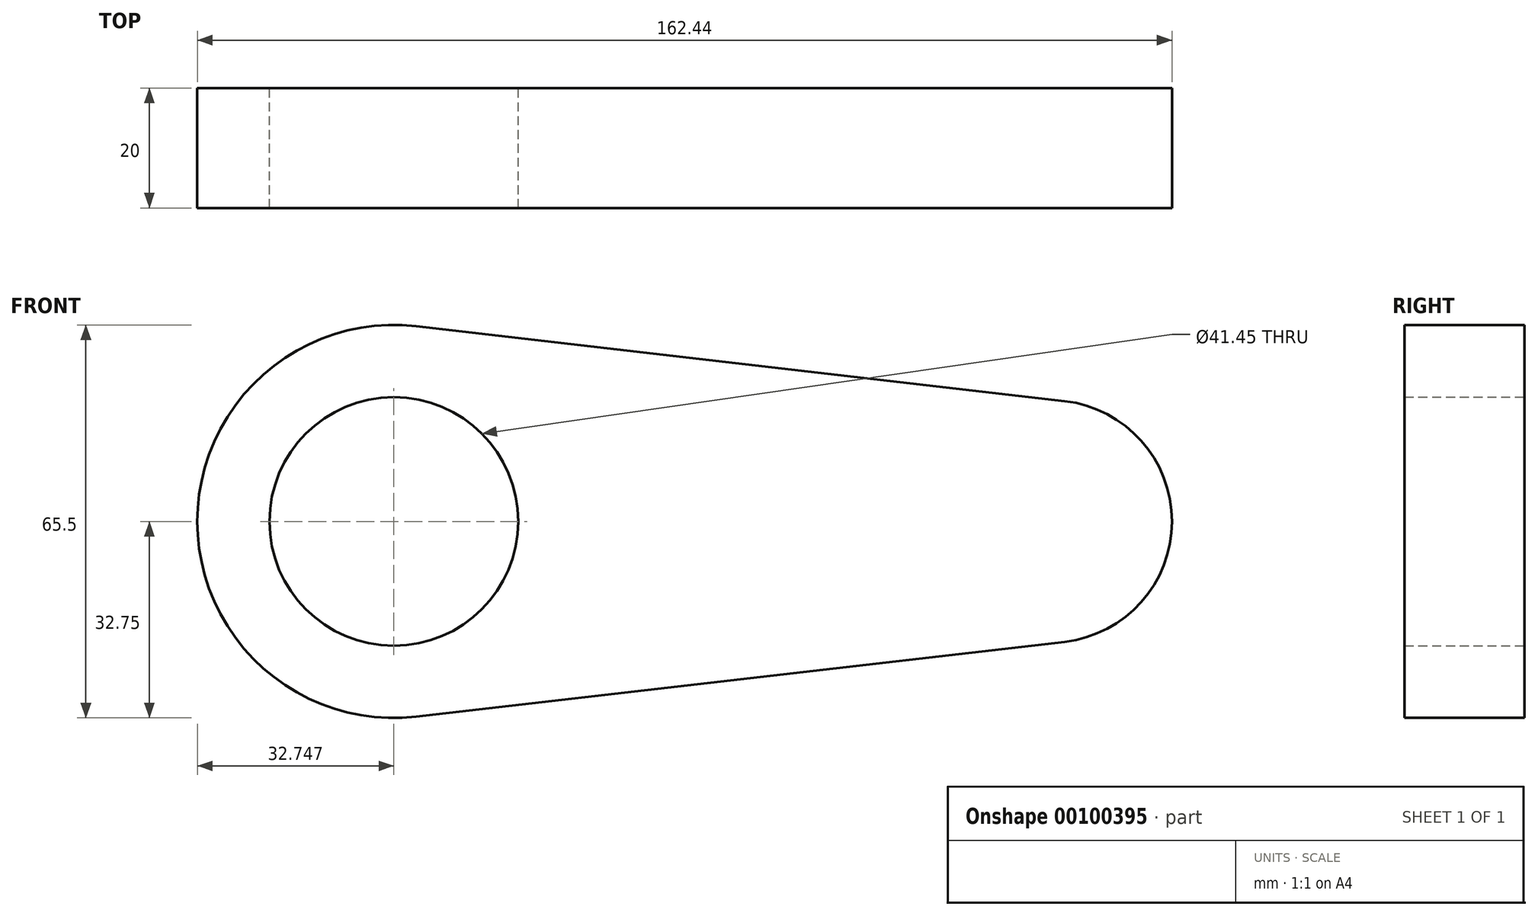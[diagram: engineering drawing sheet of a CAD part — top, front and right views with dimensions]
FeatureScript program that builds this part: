
annotation { "Feature Type Name" : "Feature", "Feature Type Description" : "" }
export const myFeature = defineFeature(function(context is Context, id is Id, definition is map)
    precondition{}
    {
        {
            var Q0;
            Q0=qCreatedBy(makeId("Front.planeOp"),FACE);
            var sketch = newSketch(context, id + "F0", { "sketchPlane" : qUnion([Q0])});
            skCircle(sketch, "E0", {"center": v(-65.7, 0) * mm, "radius": 20.72 * mm});
            skCircle(sketch, "E1", {"center": v(-65.7, 0) * mm, "radius": 32.75 * mm});
            skCircle(sketch, "E2", {"center": v(43.8, 0) * mm, "radius": 20.2 * mm});
            skLineSegment(sketch, "E3", {"start": v(-61.94, 32.53) * mm, "end": v(46.11, 20.07) * mm});
            skLineSegment(sketch, "E4", {"start": v(-61.94, -32.53) * mm, "end": v(46.11, -20.07) * mm});
            skSolve(sketch);
        }
        {
            var Q0;
            Q0 = qSketchRegion(id + "F0", true);
            extrude(context, id + "F1", {"entities" : qUnion([Q0]), "endBound" : BoundingType.SYMMETRIC, "depth" : 20 * mm});
        }
    });
